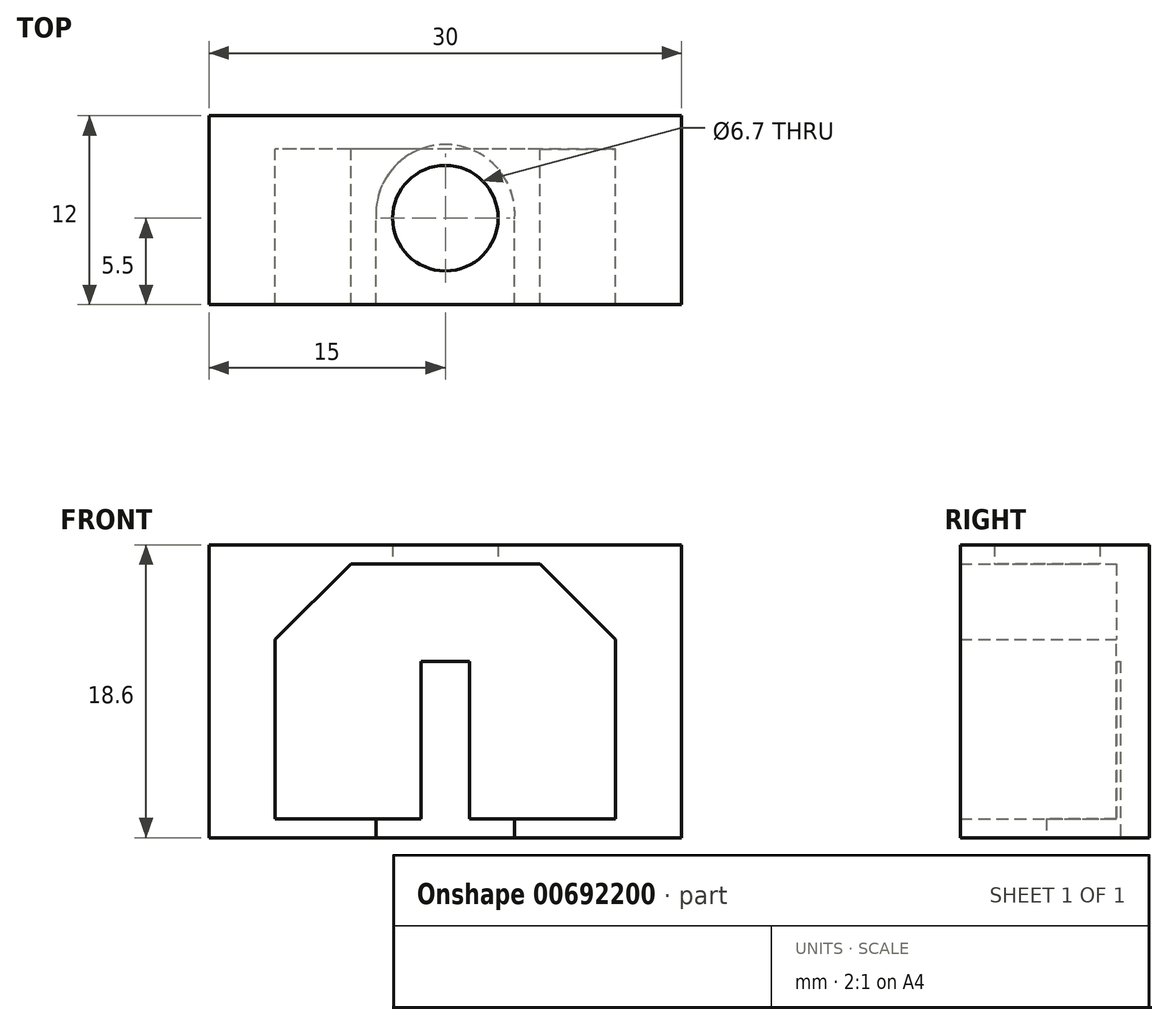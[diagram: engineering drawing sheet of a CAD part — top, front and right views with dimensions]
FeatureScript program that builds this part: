
annotation { "Feature Type Name" : "Feature", "Feature Type Description" : "" }
export const myFeature = defineFeature(function(context is Context, id is Id, definition is map)
    precondition{}
    {
        {
            var Q0;
            Q0=qCreatedBy(makeId("Front.planeOp"),FACE);
            var sketch = newSketch(context, id + "F0", { "sketchPlane" : qUnion([Q0])});
            skLineSegment(sketch, "E0.bottom", {"start": v(0, 0) * mm, "end": v(-30, 0) * mm});
            skLineSegment(sketch, "E0.top", {"start": v(0, 18.6) * mm, "end": v(-30, 18.6) * mm});
            skLineSegment(sketch, "E0.left", {"start": v(0, 0) * mm, "end": v(0, 18.6) * mm});
            skLineSegment(sketch, "E0.right", {"start": v(-30, 0) * mm, "end": v(-30, 18.6) * mm});
            skLineSegment(sketch, "E1", {"start": v(-15, 18.6) * mm, "end": v(-15, 0) * mm, "construction": true});
            skLineSegment(sketch, "E2", {"start": v(-30, 9.3) * mm, "end": v(0, 9.3) * mm, "construction": true});
            skLineSegment(sketch, "E3", {"start": v(-15, 17.4) * mm, "end": v(-25.8, 17.4) * mm});
            skLineSegment(sketch, "E4", {"start": v(-25.8, 17.4) * mm, "end": v(-25.8, 9.3) * mm});
            skLineSegment(sketch, "E5.MirrorCS", {"start": v(-4.2, 17.4) * mm, "end": v(-4.2, 9.3) * mm});
            skLineSegment(sketch, "E6.MirrorCS", {"start": v(-15, 17.4) * mm, "end": v(-4.2, 17.4) * mm});
            skLineSegment(sketch, "E7.MirrorCS", {"start": v(-4.2, 1.2) * mm, "end": v(-4.2, 9.3) * mm});
            skLineSegment(sketch, "E8.MirrorCS", {"start": v(-15, 1.2) * mm, "end": v(-4.2, 1.2) * mm});
            skLineSegment(sketch, "E9.MirrorCS", {"start": v(-15, 1.2) * mm, "end": v(-25.8, 1.2) * mm});
            skLineSegment(sketch, "E10.MirrorCS", {"start": v(-25.8, 1.2) * mm, "end": v(-25.8, 9.3) * mm});
            skLineSegment(sketch, "E11", {"start": v(-21, 17.4) * mm, "end": v(-25.8, 12.6) * mm});
            skLineSegment(sketch, "E12.MirrorCS", {"start": v(-9, 17.4) * mm, "end": v(-4.2, 12.6) * mm});
            skSolve(sketch);
        }
        {
            var Q0;
            Q0=makeQuery(id+"F0.imprint","IMPRINT",FACE,{"disambiguationData":[TD([[makeQuery(id+"F0.imprint","IMPRINT",EDGE,{"derivedFrom":sQuery(id+"F0.wireOp",EDGE,"E0.bottom")}),-1.0]])]});
            var Q1;
            {var subQ3=sQuery(id+"F0.wireOp",EDGE,"E11");Q1=makeQuery(id+"F0.imprint","IMPRINT",FACE,{"disambiguationData":[TD([[makeQuery(id+"F0.imprint","IMPRINT",EDGE,{"derivedFrom":subQ3}),-1.0]])]});}
            var Q2;
            {var subQ3=sQuery(id+"F0.wireOp",EDGE,"E12.MirrorCS");Q2=makeQuery(id+"F0.imprint","IMPRINT",FACE,{"disambiguationData":[TD([[makeQuery(id+"F0.imprint","IMPRINT",EDGE,{"derivedFrom":subQ3}),1.0]])]});}
            extrude(context, id + "F1", {"entities" : qUnion([Q0, Q1, Q2]), "depth" : 12 * mm, "offsetDistance" : 25 * mm});
        }
        {
            var Q0;
            Q0=qCreatedBy(makeId("Top.planeOp"),FACE);
            var sketch = newSketch(context, id + "F2", { "sketchPlane" : qUnion([Q0])});
            skLineSegment(sketch, "E13", {"start": v(-15, 0) * mm, "end": v(-15, -14.4) * mm, "construction": true});
            skCircle(sketch, "E14", {"center": v(-15, -6.5) * mm, "radius": 3.35 * mm});
            skLineSegment(sketch, "E15", {"start": v(-18.35, -15.29) * mm, "end": v(-15, -14.4) * mm});
            skLineSegment(sketch, "E16.MirrorCS", {"start": v(-11.65, -15.29) * mm, "end": v(-15, -14.4) * mm});
            skCircle(sketch, "E17", {"center": v(-15, -6.5) * mm, "radius": 4.4 * mm});
            skLineSegment(sketch, "E18", {"start": v(-19.4, -6.55) * mm, "end": v(-19.4, -14.93) * mm});
            skLineSegment(sketch, "E19", {"start": v(-19.4, -14.93) * mm, "end": v(-18.35, -15.29) * mm});
            skLineSegment(sketch, "E20.MirrorCS", {"start": v(-10.6, -6.55) * mm, "end": v(-10.6, -14.93) * mm});
            skLineSegment(sketch, "E21.MirrorCS", {"start": v(-10.6, -14.93) * mm, "end": v(-11.65, -15.29) * mm});
            skArc(sketch, "E22", {"start": v(-10.6, -6.55) * mm, "mid": v(-15, -1.82) * mm, "end": v(-19.4, -6.55) * mm});
            skSolve(sketch);
        }
        {
            var Q0;
            Q0=makeQuery(id+"F2.imprint","IMPRINT",FACE,{"disambiguationData":[TD([[makeQuery(id+"F2.imprint","IMPRINT",EDGE,{"derivedFrom":sQuery(id+"F2.wireOp",EDGE,"E14")}),1.0]])]});
            extrude(context, id + "F3", {"entities" : qUnion([Q0]), "operationType" : NewBodyOperationType.REMOVE, "depth" : 35.2 * mm, "offsetDistance" : 25 * mm, "hasSecondDirection" : true, "secondDirectionOppositeDirection" : false, "secondDirectionDepth" : 7.4 * mm});
        }
        {
            var Q0;
            {var subQ7=sQuery(id+"F0.wireOp",EDGE,"E7.MirrorCS");Q0=makeQuery(id+"F0.imprint","IMPRINT",FACE,{"disambiguationData":[TD([[makeQuery(id+"F0.imprint","IMPRINT",EDGE,{"derivedFrom":subQ7}),1.0]])]});}
            extrude(context, id + "F4", {"entities" : qUnion([Q0]), "operationType" : NewBodyOperationType.ADD, "depth" : 2.1 * mm, "offsetDistance" : 25 * mm});
        }
        {
            var Q0;
            Q0 = qSketchRegion(id + "F2", true);
            var Q1;
            Q1=makeQuery(id+"F2.imprint","IMPRINT",FACE,{"disambiguationData":[TD([[makeQuery(id+"F2.imprint","IMPRINT",EDGE,{"derivedFrom":sQuery(id+"F2.wireOp",EDGE,"E14")}),1.0]])]});
            extrude(context, id + "F5", {"entities" : qUnion([Q0, Q1]), "operationType" : NewBodyOperationType.REMOVE, "depth" : 11.2 * mm, "offsetDistance" : 25 * mm});
        }
    });
